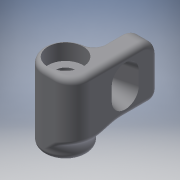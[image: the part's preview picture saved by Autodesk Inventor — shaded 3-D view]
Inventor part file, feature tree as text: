
AUTODESK INVENTOR PART (.ipt)
format: ipt  version: 2016 (Build 200138000, 138)  size: 300,544 bytes
history: native  units: mm
features: fillet x7, sketch x6, projected_geometry x5, extrude x4, loft x1
ambient origin geometry x8: Origin, YZ Plane, XZ Plane, XY Plane, X Axis, Y Axis, Z Axis, Center Point
bodies: Body1 (feature_tree)
feature tree (23):
  extrude  "Extrusion7"  Depth=8.0mm
  extrude  "Extrusion12"  Depth=4.0mm
  extrude  "Extrusion13"  Depth=4.0mm TaperAngle=0.0deg
  extrude  "Extrusion14"  Depth=3.0mm TaperAngle=0.0deg
  loft  "Loft4"
  fillet  "Fillet5"  Radius=2.5mm
  fillet  "Fillet6"  Radius=3.0mm
  fillet  "Fillet7"  Radius=6.0mm
  fillet  "Fillet8"  Radius=5.0mm
  fillet  "Fillet9"  Radius=2.76mm
  fillet  "Fillet10"  Radius=2.0mm
  fillet  "Fillet11"  Radius=1.47mm
  sketch  "Sketch10"  dims[d51=8.0mm d52=8.0mm]
  sketch  "Sketch15"  dims[d53=4.0mm d56=1.25mm]
  sketch  "Sketch16"  dims[d57=10.0mm d58=0.0mm d69=4.0mm d70=0.0mm]
  sketch  "Sketch17"  dims[d71=6.5mm d72=3.0mm d73=0.0mm]
  projected_geometry  "Projected Loop10"
  sketch  "Sketch18"  dims[d74=3.5mm d75=11.0mm d76=0.0mm d77=2.5mm d78=3.0mm d79=6.0mm d80=5.0mm d83=2.76mm d84=2.0mm d85=1.47mm]
  projected_geometry  "Projected Loop11"
  sketch  "Sketch19"  dims[d86=2.81mm d87=3.26mm d88=1.0mm d89=1.0mm d90=1.0mm d95=0.0mm d96=90.0deg d97=0.0mm d98=90.0deg]
  projected_geometry  "Projected Loop12"
  projected_geometry  "Project Cut Edges1"
  projected_geometry  "Project Cut Edges2"
